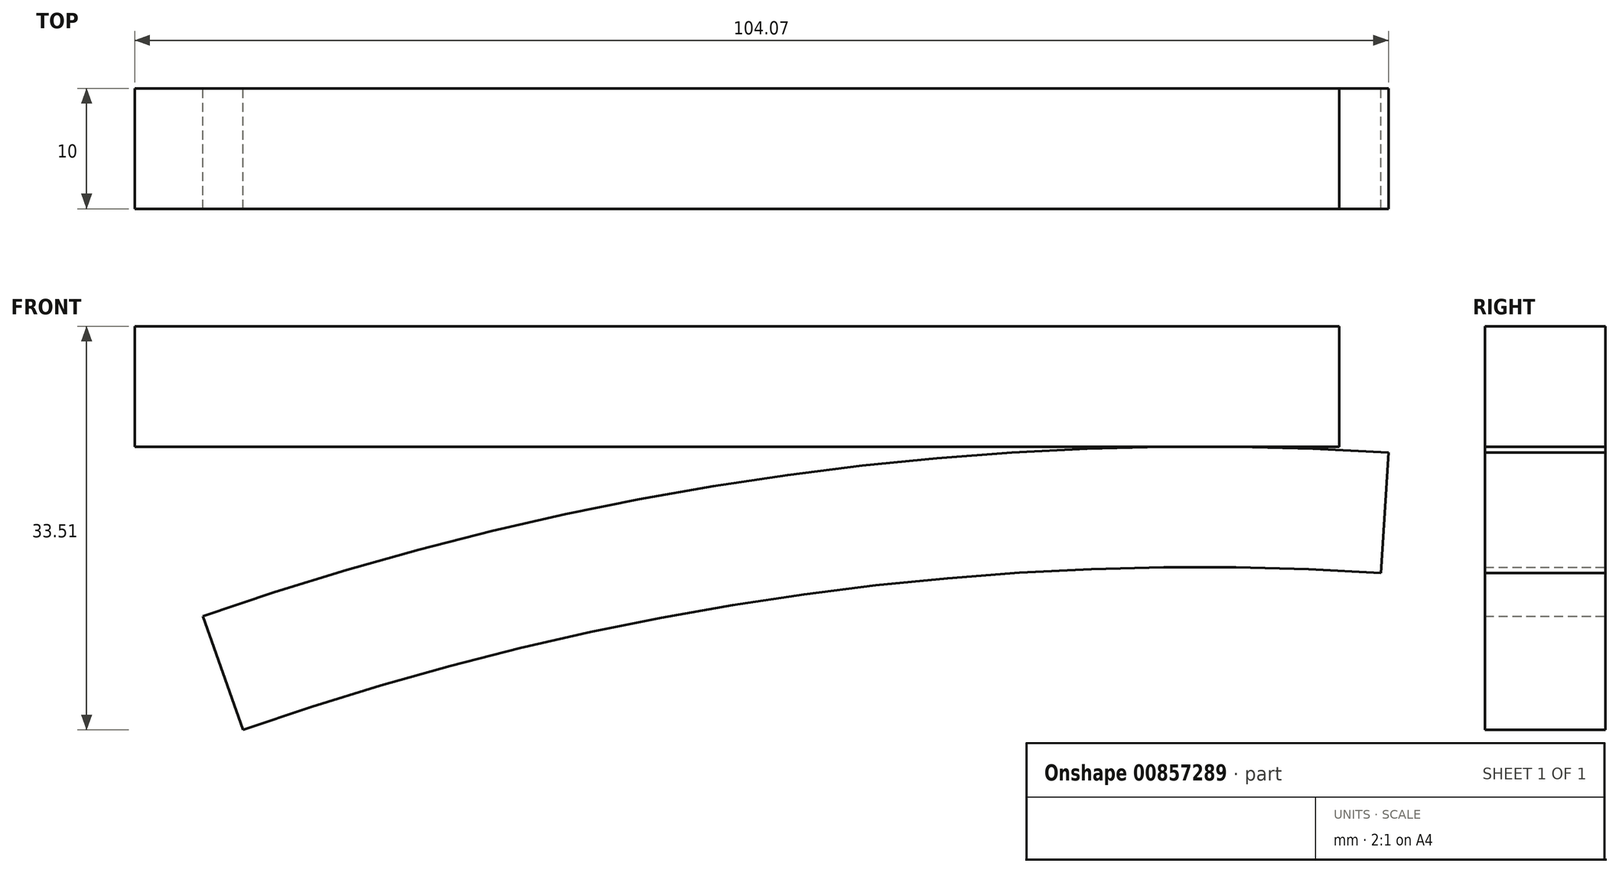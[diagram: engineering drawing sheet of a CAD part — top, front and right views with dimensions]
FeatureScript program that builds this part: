
annotation { "Feature Type Name" : "Feature", "Feature Type Description" : "" }
export const myFeature = defineFeature(function(context is Context, id is Id, definition is map)
    precondition{}
    {
        {
            var Q0;
            Q0=qCreatedBy(makeId("Front.planeOp"),FACE);
            var sketch = newSketch(context, id + "F0", { "sketchPlane" : qUnion([Q0])});
            skLineSegment(sketch, "E0.bottom", {"start": v(0, 0) * mm, "end": v(100, 0) * mm});
            skLineSegment(sketch, "E0.top", {"start": v(0, 10) * mm, "end": v(100, 10) * mm});
            skLineSegment(sketch, "E0.left", {"start": v(0, 0) * mm, "end": v(0, 10) * mm});
            skLineSegment(sketch, "E0.right", {"start": v(100, 0) * mm, "end": v(100, 10) * mm});
            skArc(sketch, "E1", {"start": v(104.07, -0.5) * mm, "mid": v(54.19, -2.35) * mm, "end": v(5.67, -14.08) * mm});
            skLineSegment(sketch, "E2", {"start": v(103.44, -10.47) * mm, "end": v(104.07, -0.5) * mm});
            skLineSegment(sketch, "E3", {"start": v(88.37, -250) * mm, "end": v(5.67, -14.08) * mm});
            skArc(sketch, "E4", {"start": v(103.44, -10.47) * mm, "mid": v(55.55, -12.25) * mm, "end": v(8.98, -23.51) * mm});
            skSolve(sketch);
        }
        {
            var Q0;
            Q0=makeQuery(id+"F0.imprint","IMPRINT",FACE,{"disambiguationData":[TD([[makeQuery(id+"F0.imprint","IMPRINT",EDGE,{"derivedFrom":sQuery(id+"F0.wireOp",EDGE,"E0.top")}),-1.0]])]});
            extrude(context, id + "F1", {"entities" : qUnion([Q0]), "depth" : 10 * mm, "offsetDistance" : 25 * mm});
        }
        {
            var Q0;
            Q0 = qSketchRegion(id + "F0", true);
            extrude(context, id + "F2", {"entities" : qUnion([Q0]), "depth" : 10 * mm, "offsetDistance" : 25 * mm});
        }
    });
